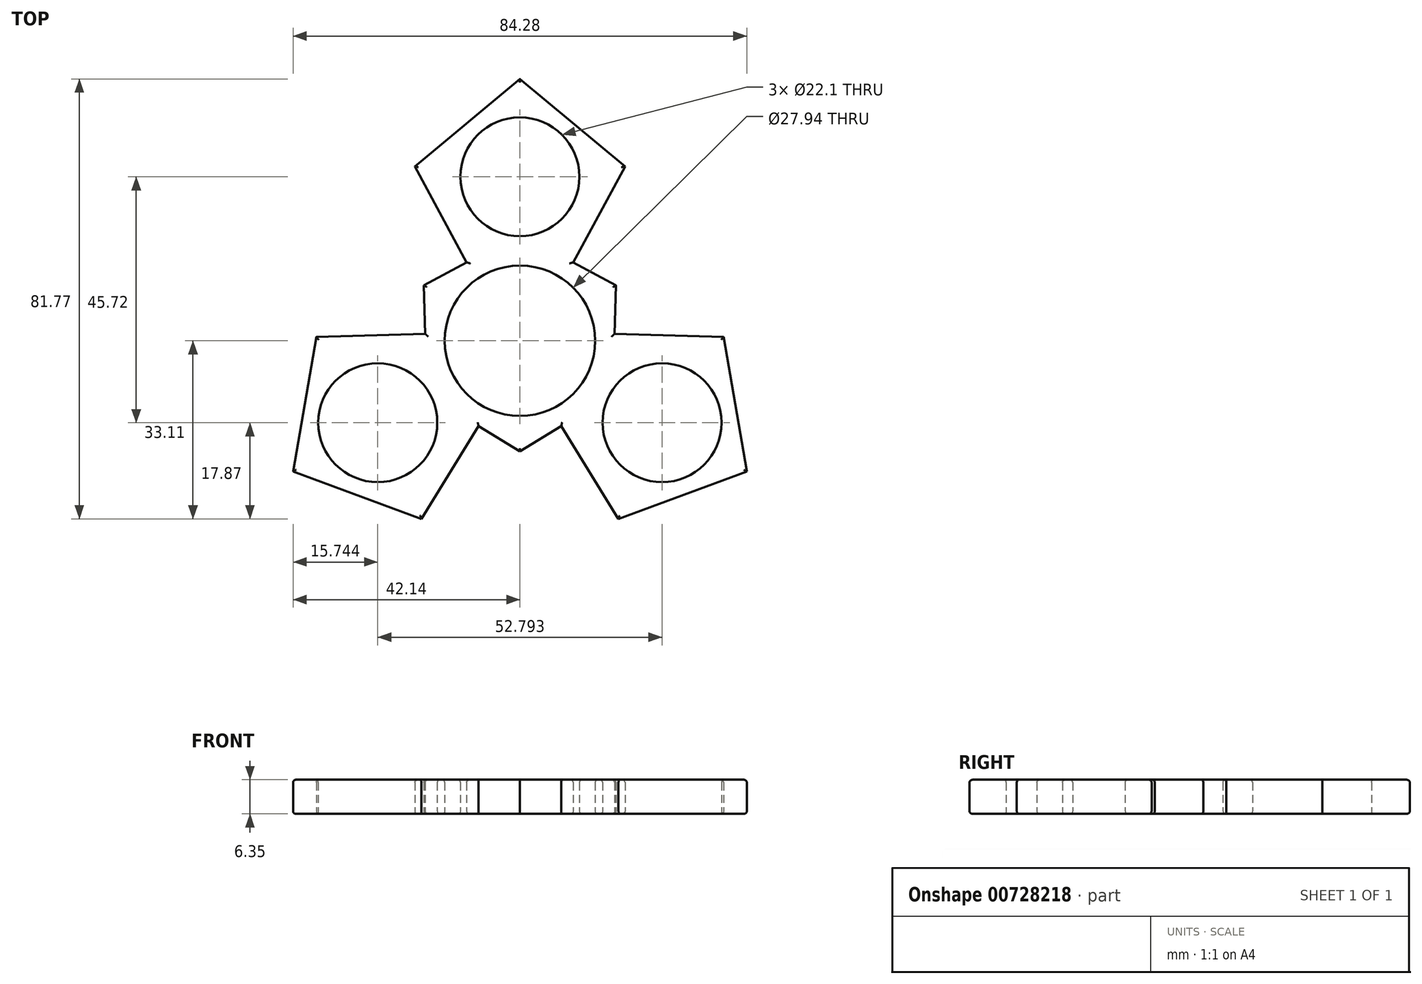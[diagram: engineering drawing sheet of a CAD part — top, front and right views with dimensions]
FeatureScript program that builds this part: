
annotation { "Feature Type Name" : "Feature", "Feature Type Description" : "" }
export const myFeature = defineFeature(function(context is Context, id is Id, definition is map)
    precondition{}
    {
        {
            var Q0;
            Q0=qCreatedBy(makeId("Top.planeOp"),FACE);
            var sketch = newSketch(context, id + "F0", { "sketchPlane" : qUnion([Q0])});
            skCircle(sketch, "E0", {"center": v(0, 0) * mm, "radius": 11.05 * mm});
            skCircle(sketch, "E1", {"center": v(0, 0) * mm, "radius": 13.97 * mm});
            skCircle(sketch, "E2", {"center": v(0, 30.48) * mm, "radius": 11.05 * mm});
            skCircle(sketch, "E3", {"center": v(0, 30.48) * mm, "radius": 13.97 * mm});
            skCircle(sketch, "E4.1.0", {"center": v(-26.4, -15.24) * mm, "radius": 13.97 * mm});
            skCircle(sketch, "E4.1.1", {"center": v(-26.4, -15.24) * mm, "radius": 11.05 * mm});
            skCircle(sketch, "E4.2.0", {"center": v(26.4, -15.24) * mm, "radius": 13.97 * mm});
            skCircle(sketch, "E4.2.1", {"center": v(26.4, -15.24) * mm, "radius": 11.05 * mm});
            skArc(sketch, "E5", {"start": v(-26.4, -1.27) * mm, "mid": v(-12.1, 6.98) * mm, "end": v(-12.1, 23.5) * mm});
            skArc(sketch, "E6.1.0", {"start": v(14.3, -22.23) * mm, "mid": v(0, -13.97) * mm, "end": v(-14.3, -22.23) * mm});
            skArc(sketch, "E6.2.0", {"start": v(12.1, 23.5) * mm, "mid": v(12.1, 6.98) * mm, "end": v(26.4, -1.27) * mm});
            skLineSegment(sketch, "E7", {"start": v(0, 48.66) * mm, "end": v(19.52, 32.4) * mm});
            skLineSegment(sketch, "E8", {"start": v(19.52, 32.4) * mm, "end": v(0, 48.66) * mm});
            skLineSegment(sketch, "E9", {"start": v(0, 48.66) * mm, "end": v(-19.52, 32.4) * mm});
            skLineSegment(sketch, "E10", {"start": v(-19.52, 32.4) * mm, "end": v(-9.9, 14.58) * mm});
            skLineSegment(sketch, "E11", {"start": v(19.52, 32.4) * mm, "end": v(9.9, 14.58) * mm});
            skLineSegment(sketch, "E12.1.0", {"start": v(-18.3, -33.1) * mm, "end": v(-7.68, -15.86) * mm});
            skLineSegment(sketch, "E12.1.1", {"start": v(-42.14, -24.33) * mm, "end": v(-18.3, -33.1) * mm});
            skLineSegment(sketch, "E12.1.2", {"start": v(-37.82, 0.7) * mm, "end": v(-42.14, -24.33) * mm});
            skLineSegment(sketch, "E12.1.3", {"start": v(-37.82, 0.7) * mm, "end": v(-17.58, 1.28) * mm});
            skLineSegment(sketch, "E12.2.0", {"start": v(37.82, 0.7) * mm, "end": v(17.58, 1.28) * mm});
            skLineSegment(sketch, "E12.2.1", {"start": v(42.14, -24.33) * mm, "end": v(37.82, 0.7) * mm});
            skLineSegment(sketch, "E12.2.2", {"start": v(18.3, -33.1) * mm, "end": v(42.14, -24.33) * mm});
            skLineSegment(sketch, "E12.2.3", {"start": v(18.3, -33.1) * mm, "end": v(7.68, -15.86) * mm});
            skLineSegment(sketch, "E13", {"start": v(-7.68, -15.86) * mm, "end": v(0, -20.6) * mm});
            skLineSegment(sketch, "E14", {"start": v(0, -20.6) * mm, "end": v(7.68, -15.86) * mm});
            skLineSegment(sketch, "E15.1.0", {"start": v(17.58, 1.28) * mm, "end": v(17.84, 10.3) * mm});
            skLineSegment(sketch, "E15.1.1", {"start": v(17.84, 10.3) * mm, "end": v(9.9, 14.58) * mm});
            skLineSegment(sketch, "E15.2.0", {"start": v(-9.9, 14.58) * mm, "end": v(-17.84, 10.3) * mm});
            skLineSegment(sketch, "E15.2.1", {"start": v(-17.84, 10.3) * mm, "end": v(-17.58, 1.28) * mm});
            skSolve(sketch);
        }
        {
            var Q0;
            Q0=qSketchRegion(id+"F0",true);
            extrude(context, id + "F1", {"entities" : qUnion([Q0]), "depth" : 6.35 * mm, "offsetDistance" : 25.4 * mm});
        }
        {
            var Q0;
            Q0=makeQuery(id+"F1.opExtrude","CAP_FACE",FACE,{"disambiguationData":[OSD([sQuery(id+"F0.wireOp",EDGE,"E1"),sQuery(id+"F0.wireOp",EDGE,"E2"),sQuery(id+"F0.wireOp",EDGE,"E4.1.1"),sQuery(id+"F0.wireOp",EDGE,"E4.2.1"),sQuery(id+"F0.wireOp",EDGE,"E8"),sQuery(id+"F0.wireOp",EDGE,"E9"),sQuery(id+"F0.wireOp",EDGE,"E10"),sQuery(id+"F0.wireOp",EDGE,"E11"),sQuery(id+"F0.wireOp",EDGE,"E12.1.0"),sQuery(id+"F0.wireOp",EDGE,"E12.1.1"),sQuery(id+"F0.wireOp",EDGE,"E12.1.2"),sQuery(id+"F0.wireOp",EDGE,"E12.1.3"),sQuery(id+"F0.wireOp",EDGE,"E12.2.0"),sQuery(id+"F0.wireOp",EDGE,"E12.2.1"),sQuery(id+"F0.wireOp",EDGE,"E12.2.2"),sQuery(id+"F0.wireOp",EDGE,"E12.2.3"),sQuery(id+"F0.wireOp",EDGE,"E13"),sQuery(id+"F0.wireOp",EDGE,"E14"),sQuery(id+"F0.wireOp",EDGE,"E15.1.0"),sQuery(id+"F0.wireOp",EDGE,"E15.1.1"),sQuery(id+"F0.wireOp",EDGE,"E15.2.0"),sQuery(id+"F0.wireOp",EDGE,"E15.2.1")])],"isStart":true});
            var Q1;
            Q1=makeQuery(id+"F1.opExtrude","CAP_FACE",FACE,{"disambiguationData":[OSD([sQuery(id+"F0.wireOp",EDGE,"E1"),sQuery(id+"F0.wireOp",EDGE,"E2"),sQuery(id+"F0.wireOp",EDGE,"E4.1.1"),sQuery(id+"F0.wireOp",EDGE,"E4.2.1"),sQuery(id+"F0.wireOp",EDGE,"E8"),sQuery(id+"F0.wireOp",EDGE,"E9"),sQuery(id+"F0.wireOp",EDGE,"E10"),sQuery(id+"F0.wireOp",EDGE,"E11"),sQuery(id+"F0.wireOp",EDGE,"E12.1.0"),sQuery(id+"F0.wireOp",EDGE,"E12.1.1"),sQuery(id+"F0.wireOp",EDGE,"E12.1.2"),sQuery(id+"F0.wireOp",EDGE,"E12.1.3"),sQuery(id+"F0.wireOp",EDGE,"E12.2.0"),sQuery(id+"F0.wireOp",EDGE,"E12.2.1"),sQuery(id+"F0.wireOp",EDGE,"E12.2.2"),sQuery(id+"F0.wireOp",EDGE,"E12.2.3"),sQuery(id+"F0.wireOp",EDGE,"E13"),sQuery(id+"F0.wireOp",EDGE,"E14"),sQuery(id+"F0.wireOp",EDGE,"E15.1.0"),sQuery(id+"F0.wireOp",EDGE,"E15.1.1"),sQuery(id+"F0.wireOp",EDGE,"E15.2.0"),sQuery(id+"F0.wireOp",EDGE,"E15.2.1")])],"isStart":false});
            fillet(context, id + "F2", {"entities" : qUnion([Q0, Q1]), "radius" : 0.5 * mm, "tangentPropagation" : true, "allowEdgeOverflow" : false});
        }
    });
